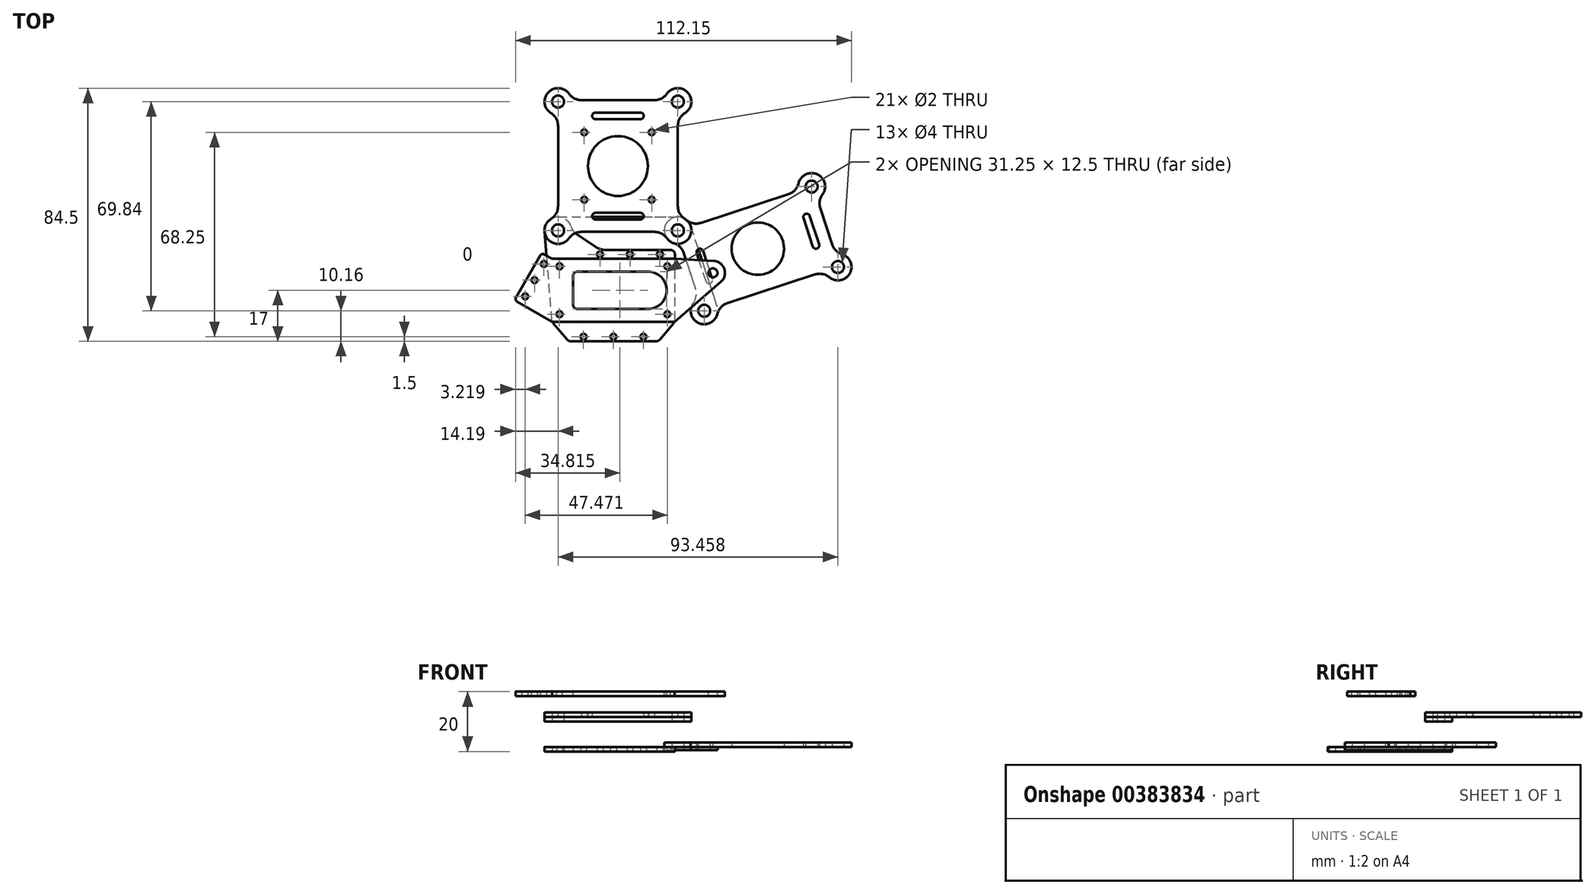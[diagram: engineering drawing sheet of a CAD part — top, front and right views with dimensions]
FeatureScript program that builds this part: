
annotation { "Feature Type Name" : "Feature", "Feature Type Description" : "" }
export const myFeature = defineFeature(function(context is Context, id is Id, definition is map)
    precondition{}
    {
        {
            var Q0;
            Q0=qCreatedBy(makeId("Top.planeOp"),FACE);
            var sketch = newSketch(context, id + "F0", { "sketchPlane" : qUnion([Q0])});
            skArc(sketch, "E0", {"start": v(0, -6.25) * mm, "mid": v(6.25, 0) * mm, "end": v(0, 6.25) * mm});
            skCircle(sketch, "E1", {"center": v(6.5, 8) * mm, "radius": 1 * mm});
            skLineSegment(sketch, "E2", {"start": v(6.5, 8) * mm, "end": v(-29.5, 8) * mm, "construction": true});
            skPoint(sketch, "E3", {"position": v(-11.5, 8) * mm});
            skCircle(sketch, "E4", {"center": v(-29.5, 8) * mm, "radius": 1 * mm});
            skCircle(sketch, "E5.MirrorC", {"center": v(-29.5, -8) * mm, "radius": 1 * mm});
            skCircle(sketch, "E6.MirrorC", {"center": v(6.5, -8) * mm, "radius": 1 * mm});
            skLineSegment(sketch, "E7.bottom", {"start": v(-32, 10.5) * mm, "end": v(9, 10.5) * mm});
            skLineSegment(sketch, "E7.top", {"start": v(-32, -10.5) * mm, "end": v(9, -10.5) * mm});
            skLineSegment(sketch, "E7.left", {"start": v(-32, 10.5) * mm, "end": v(-32, -10.5) * mm});
            skLineSegment(sketch, "E7.right", {"start": v(9, 10.5) * mm, "end": v(9, -10.5) * mm});
            skPoint(sketch, "E7.middle", {"position": v(-11.5, 0) * mm});
            skLineSegment(sketch, "E8", {"start": v(0, 0) * mm, "end": v(18.8, -6.84) * mm, "construction": true});
            skCircle(sketch, "E9", {"center": v(-30, 20) * mm, "radius": 2 * mm});
            skLineSegment(sketch, "E10", {"start": v(-30, 20) * mm, "end": v(10, 20) * mm, "construction": true});
            skLineSegment(sketch, "E11", {"start": v(10, 20) * mm, "end": v(18.8, -6.84) * mm, "construction": true});
            skCircle(sketch, "E12", {"center": v(10, 20) * mm, "radius": 2 * mm});
            skCircle(sketch, "E13", {"center": v(18.8, -6.84) * mm, "radius": 2 * mm});
            skCircle(sketch, "E14", {"center": v(18.8, -6.84) * mm, "radius": 4.5 * mm});
            skCircle(sketch, "E15", {"center": v(10, 20) * mm, "radius": 4.5 * mm});
            skLineSegment(sketch, "E16", {"start": v(10, 20) * mm, "end": v(14.28, 21.4) * mm, "construction": true});
            skLineSegment(sketch, "E17", {"start": v(14.28, 21.4) * mm, "end": v(23.07, -5.44) * mm});
            skLineSegment(sketch, "E18", {"start": v(10.92, 15.6) * mm, "end": v(16.93, -2.75) * mm});
            skCircle(sketch, "E19", {"center": v(-30, 20) * mm, "radius": 4.5 * mm});
            skLineSegment(sketch, "E20", {"start": v(-32, -10.5) * mm, "end": v(-34.48, 19.63) * mm});
            skLineSegment(sketch, "E21", {"start": v(-15.92, 13.5) * mm, "end": v(-25.5, 20) * mm});
            skLineSegment(sketch, "E22", {"start": v(0, 6.25) * mm, "end": v(-23.5, 6.25) * mm});
            skLineSegment(sketch, "E23", {"start": v(-25, 4.75) * mm, "end": v(-25, 0) * mm});
            skLineSegment(sketch, "E24.MirrorCS", {"start": v(-25, -4.75) * mm, "end": v(-25, 0) * mm});
            skLineSegment(sketch, "E25.MirrorCS", {"start": v(0, -6.25) * mm, "end": v(-23.5, -6.25) * mm});
            skPoint(sketch, "E26.visualSharp", {"position": v(-25, 6.25) * mm});
            skArc(sketch, "E26.filletArc", {"start": v(-23.5, 6.25) * mm, "mid": v(-24.56, 5.81) * mm, "end": v(-25, 4.75) * mm});
            skPoint(sketch, "E27.visualSharp", {"position": v(-25, -6.25) * mm});
            skArc(sketch, "E27.filletArc", {"start": v(-25, -4.75) * mm, "mid": v(-24.56, -5.81) * mm, "end": v(-23.5, -6.25) * mm});
            skPoint(sketch, "E28.visualSharp", {"position": v(0, 6.25) * mm});
            skLineSegment(sketch, "E28.filletArc", {"start": v(0, 6.25) * mm, "end": v(0, 6.25) * mm});
            skPoint(sketch, "E29.visualSharp", {"position": v(0, -6.25) * mm});
            skLineSegment(sketch, "E29.filletArc", {"start": v(0, -6.25) * mm, "end": v(0, -6.25) * mm});
            skLineSegment(sketch, "E30.bottom", {"start": v(-26.5, -10.5) * mm, "end": v(3.5, -10.5) * mm});
            skLineSegment(sketch, "E30.top", {"start": v(-26.5, -17) * mm, "end": v(3.5, -17) * mm});
            skLineSegment(sketch, "E30.left", {"start": v(-26.5, -10.5) * mm, "end": v(-26.5, -17) * mm});
            skLineSegment(sketch, "E30.right", {"start": v(3.5, -10.5) * mm, "end": v(3.5, -17) * mm});
            skPoint(sketch, "E30.middle", {"position": v(-11.5, -13.75) * mm});
            skLineSegment(sketch, "E31", {"start": v(-32, -10.5) * mm, "end": v(-26.5, -17) * mm});
            skLineSegment(sketch, "E32", {"start": v(3.5, -17) * mm, "end": v(9, -10.5) * mm});
            skLineSegment(sketch, "E33", {"start": v(-11.5, -10.5) * mm, "end": v(-11.5, -17) * mm, "construction": true});
            skCircle(sketch, "E34", {"center": v(4, 12) * mm, "radius": 1 * mm});
            skCircle(sketch, "E35", {"center": v(-6, 12) * mm, "radius": 1 * mm});
            skCircle(sketch, "E36", {"center": v(-16, 12) * mm, "radius": 1 * mm});
            skLineSegment(sketch, "E37", {"start": v(9, 10.5) * mm, "end": v(9, 13.5) * mm});
            skLineSegment(sketch, "E38", {"start": v(9, 13.5) * mm, "end": v(-15.92, 13.5) * mm});
            skPoint(sketch, "E39.orphan", {"position": v(-11.5, 10.5) * mm});
            skCircle(sketch, "E40", {"center": v(-11.5, -15.5) * mm, "radius": 1 * mm});
            skCircle(sketch, "E41", {"center": v(-1.5, -15.5) * mm, "radius": 1 * mm});
            skCircle(sketch, "E42.MirrorC", {"center": v(-21.5, -15.5) * mm, "radius": 1 * mm});
            skSolve(sketch);
        }
        {
            var Q0;
            Q0=qSketchRegion(id+"F0",true);
            extrude(context, id + "F1", {"entities" : qUnion([Q0]), "depth" : 1.5 * mm, "offsetDistance" : 25 * mm});
        }
        {
            var Q0;
            Q0=qCreatedBy(makeId("Top.planeOp"),FACE);
            cPlane(context, id + "F2", {"entities" : qUnion([Q0]), "cplaneType" : CPlaneType.OFFSET, "offset" : 10 * mm, "width" : 150 * mm, "height" : 150 * mm});
        }
        {
            var Q0;
            Q0=qCreatedBy(id+"F2.planeOp",FACE);
            var sketch = newSketch(context, id + "F3", { "sketchPlane" : qUnion([Q0])});
            skCircle(sketch, "E43.0", {"center": v(10, 20) * mm, "radius": 2 * mm});
            skCircle(sketch, "E44.0", {"center": v(-30, 20) * mm, "radius": 2 * mm});
            skArc(sketch, "E45", {"start": v(-30, 24.5) * mm, "mid": v(-33.35, 17) * mm, "end": v(-25.53, 19.5) * mm});
            skArc(sketch, "E46", {"start": v(5.53, 19.5) * mm, "mid": v(13.35, 17) * mm, "end": v(10, 24.5) * mm});
            skLineSegment(sketch, "E47", {"start": v(-30, 24.5) * mm, "end": v(10, 24.5) * mm});
            skLineSegment(sketch, "E48", {"start": v(-25.53, 19.5) * mm, "end": v(5.53, 19.5) * mm});
            skSolve(sketch);
        }
        {
            var Q0;
            Q0=qSketchRegion(id+"F3",true);
            extrude(context, id + "F4", {"entities" : qUnion([Q0]), "depth" : 1.5 * mm, "offsetDistance" : 25 * mm});
        }
        {
            var Q0;
            Q0=makeQuery(id+"F1.opExtrude","SWEPT_EDGE",EDGE,{"disambiguationData":[OSD([sQuery(id+"F0.wireOp",EDGE,"E15"),sQuery(id+"F0.wireOp",EDGE,"E18")])]});
            var Q1;
            Q1=makeQuery(id+"F1.opExtrude","SWEPT_EDGE",EDGE,{"disambiguationData":[OSD([sQuery(id+"F0.wireOp",EDGE,"E14"),sQuery(id+"F0.wireOp",EDGE,"E18")])]});
            var Q2;
            Q2=makeQuery(id+"F4.opExtrude","SWEPT_EDGE",EDGE,{"disambiguationData":[OSD([sQuery(id+"F3.wireOp",EDGE,"E45"),sQuery(id+"F3.wireOp",EDGE,"E48")])]});
            var Q3;
            Q3=makeQuery(id+"F4.opExtrude","SWEPT_EDGE",EDGE,{"disambiguationData":[OSD([sQuery(id+"F3.wireOp",EDGE,"E46"),sQuery(id+"F3.wireOp",EDGE,"E48")])]});
            var Q4;
            Q4=makeQuery(id+"F1.opExtrude","SWEPT_EDGE",EDGE,{"disambiguationData":[OSD([sQuery(id+"F0.wireOp",EDGE,"E19"),sQuery(id+"F0.wireOp",EDGE,"E21")])]});
            var Q5;
            Q5=makeQuery(id+"F1.opExtrude","SWEPT_EDGE",EDGE,{"disambiguationData":[OSD([sQuery(id+"F0.wireOp",EDGE,"E7.bottom"),sQuery(id+"F0.wireOp",EDGE,"E21")])]});
            fillet(context, id + "F5", {"entities" : qUnion([Q0, Q1, Q2, Q3, Q4, Q5]), "radius" : 5 * mm, "tangentPropagation" : true, "allowEdgeOverflow" : false});
        }
        {
            var Q0;
            Q0=makeQuery(id+"F1.opExtrude","SWEPT_EDGE",EDGE,{"disambiguationData":[OSD([sQuery(id+"F0.wireOp",EDGE,"E7.bottom"),sQuery(id+"F0.wireOp",EDGE,"E7.right")])]});
            var Q1;
            Q1=makeQuery(id+"F1.opExtrude","SWEPT_EDGE",EDGE,{"disambiguationData":[OSD([sQuery(id+"F0.wireOp",EDGE,"E7.top"),sQuery(id+"F0.wireOp",EDGE,"E7.left"),sQuery(id+"F0.wireOp",EDGE,"E20")])]});
            var Q2;
            Q2=makeQuery(id+"F1.opExtrude","SWEPT_EDGE",EDGE,{"disambiguationData":[OSD([sQuery(id+"F0.wireOp",EDGE,"E7.top"),sQuery(id+"F0.wireOp",EDGE,"E7.right")])]});
            var Q3;
            Q3=makeQuery(id+"F1.opExtrude","SWEPT_EDGE",EDGE,{"disambiguationData":[OSD([sQuery(id+"F0.wireOp",EDGE,"E30.top"),sQuery(id+"F0.wireOp",EDGE,"E30.left"),sQuery(id+"F0.wireOp",EDGE,"E31")])]});
            var Q4;
            Q4=makeQuery(id+"F1.opExtrude","SWEPT_EDGE",EDGE,{"disambiguationData":[OSD([sQuery(id+"F0.wireOp",EDGE,"E30.top"),sQuery(id+"F0.wireOp",EDGE,"E30.right"),sQuery(id+"F0.wireOp",EDGE,"E32")])]});
            var Q5;
            Q5=makeQuery(id+"F1.opExtrude","SWEPT_EDGE",EDGE,{"disambiguationData":[OSD([sQuery(id+"F0.wireOp",EDGE,"E37"),sQuery(id+"F0.wireOp",EDGE,"E38")])]});
            fillet(context, id + "F6", {"entities" : qUnion([Q0, Q1, Q2, Q3, Q4, Q5]), "radius" : 1.5 * mm, "tangentPropagation" : true, "allowEdgeOverflow" : false});
        }
        {
            var Q0;
            Q0=makeQuery(id+"F1.opExtrude","CAP_FACE",FACE,{"disambiguationData":[OSD([sQuery(id+"F0.wireOp",EDGE,"E12"),sQuery(id+"F0.wireOp",EDGE,"E13"),sQuery(id+"F0.wireOp",EDGE,"E14"),sQuery(id+"F0.wireOp",EDGE,"E15"),sQuery(id+"F0.wireOp",EDGE,"E17"),sQuery(id+"F0.wireOp",EDGE,"E18")])],"isStart":true});
            extrude(context, id + "F7", {"entities" : qUnion([Q0]), "operationType" : NewBodyOperationType.REMOVE, "oppositeDirection" : true, "depth" : 0.5 * mm, "offsetDistance" : 25 * mm});
        }
        {
            var Q0;
            Q0=makeQuery(id+"F1.opExtrude","CAP_FACE",FACE,{"disambiguationData":[OSD([sQuery(id+"F0.wireOp",EDGE,"E12"),sQuery(id+"F0.wireOp",EDGE,"E13"),sQuery(id+"F0.wireOp",EDGE,"E14"),sQuery(id+"F0.wireOp",EDGE,"E15"),sQuery(id+"F0.wireOp",EDGE,"E17"),sQuery(id+"F0.wireOp",EDGE,"E18")])],"isStart":false});
            var sketch = newSketch(context, id + "F8", { "sketchPlane" : qUnion([Q0])});
            skLineSegment(sketch, "E49", {"start": v(13.92, 6.42) * mm, "end": v(36.73, 13.9) * mm, "construction": true});
            skLineSegment(sketch, "E50", {"start": v(36.73, 13.9) * mm, "end": v(41.13, 0.48) * mm, "construction": true});
            skLineSegment(sketch, "E51", {"start": v(23.07, -5.44) * mm, "end": v(41.13, 0.48) * mm});
            skPoint(sketch, "E52", {"position": v(18.8, -6.84) * mm});
            skLineSegment(sketch, "E53", {"start": v(18.8, -6.84) * mm, "end": v(23.07, -5.44) * mm, "construction": true});
            skLineSegment(sketch, "E54.MirrorCS", {"start": v(14.28, 21.4) * mm, "end": v(32.33, 27.32) * mm});
            skArc(sketch, "E55.0.0", {"start": v(14.28, 21.4) * mm, "mid": v(6.8, 23.16) * mm, "end": v(8.67, 15.7) * mm});
            skArc(sketch, "E55.0.1", {"start": v(8.67, 15.7) * mm, "mid": v(10.7, 14.49) * mm, "end": v(11.94, 12.48) * mm});
            skLineSegment(sketch, "E55.0.2", {"start": v(11.94, 12.48) * mm, "end": v(15.9, 0.36) * mm});
            skArc(sketch, "E55.0.3", {"start": v(15.9, 0.36) * mm, "mid": v(16.1, -1.99) * mm, "end": v(15.18, -4.16) * mm});
            skArc(sketch, "E55.0.4", {"start": v(15.18, -4.16) * mm, "mid": v(18.08, -11.28) * mm, "end": v(23.07, -5.44) * mm});
            skLineSegment(sketch, "E55.0.5", {"start": v(23.07, -5.44) * mm, "end": v(14.28, 21.4) * mm});
            skLineSegment(sketch, "E56.MirrorCS", {"start": v(57.55, 27.43) * mm, "end": v(61.52, 15.3) * mm});
            skArc(sketch, "E57.MirrorCS", {"start": v(58.28, 31.96) * mm, "mid": v(57.37, 29.78) * mm, "end": v(57.55, 27.43) * mm});
            skArc(sketch, "E58.MirrorCS", {"start": v(50.39, 33.23) * mm, "mid": v(55.38, 39.08) * mm, "end": v(58.28, 31.96) * mm});
            skLineSegment(sketch, "E59.MirrorCS", {"start": v(50.39, 33.23) * mm, "end": v(32.33, 27.32) * mm});
            skLineSegment(sketch, "E60.MirrorCS", {"start": v(63.46, 7.8) * mm, "end": v(59.18, 6.4) * mm, "construction": true});
            skLineSegment(sketch, "E61.MirrorCS", {"start": v(59.18, 6.4) * mm, "end": v(41.13, 0.48) * mm});
            skLineSegment(sketch, "E62.MirrorCS", {"start": v(59.54, 21.37) * mm, "end": v(36.73, 13.9) * mm, "construction": true});
            skArc(sketch, "E63.MirrorCS", {"start": v(61.52, 15.3) * mm, "mid": v(62.77, 13.3) * mm, "end": v(64.8, 12.1) * mm});
            skPoint(sketch, "E64.MirrorP", {"position": v(63.46, 7.8) * mm});
            skArc(sketch, "E65.MirrorCS", {"start": v(64.8, 12.1) * mm, "mid": v(66.66, 4.64) * mm, "end": v(59.18, 6.4) * mm});
            skLineSegment(sketch, "E66.MirrorCS", {"start": v(59.18, 6.4) * mm, "end": v(59.18, 6.4) * mm});
            skCircle(sketch, "E67.0", {"center": v(10, 20) * mm, "radius": 2 * mm});
            skCircle(sketch, "E68.0", {"center": v(18.8, -6.84) * mm, "radius": 2 * mm});
            skCircle(sketch, "E69.MirrorC", {"center": v(54.66, 34.63) * mm, "radius": 2 * mm});
            skCircle(sketch, "E70.MirrorC", {"center": v(63.46, 7.8) * mm, "radius": 2 * mm});
            skCircle(sketch, "E71", {"center": v(36.73, 13.9) * mm, "radius": 8.75 * mm});
            skLineSegment(sketch, "E72.trimOffspring", {"start": v(59.18, 6.4) * mm, "end": v(50.39, 33.23) * mm});
            skLineSegment(sketch, "E73.trimOffspring", {"start": v(14.28, 21.4) * mm, "end": v(14.28, 21.4) * mm});
            skCircle(sketch, "E74", {"center": v(53, 24.49) * mm, "radius": 1.1 * mm});
            skLineSegment(sketch, "E75", {"start": v(53, 24.49) * mm, "end": v(51.94, 24.14) * mm, "construction": true});
            skLineSegment(sketch, "E76", {"start": v(51.94, 24.14) * mm, "end": v(53.5, 19.4) * mm});
            skLineSegment(sketch, "E77", {"start": v(53, 24.49) * mm, "end": v(54.55, 19.73) * mm, "construction": true});
            skLineSegment(sketch, "E78.MirrorCS", {"start": v(54.04, 24.83) * mm, "end": v(55.6, 20.08) * mm});
            skLineSegment(sketch, "E79.MirrorCS", {"start": v(57.15, 15.33) * mm, "end": v(55.6, 20.08) * mm});
            skLineSegment(sketch, "E80.MirrorCS", {"start": v(55.06, 14.64) * mm, "end": v(53.5, 19.4) * mm});
            skCircle(sketch, "E81.MirrorC", {"center": v(56.1, 14.98) * mm, "radius": 1.1 * mm});
            skLineSegment(sketch, "E82.MirrorCS", {"start": v(56.1, 14.98) * mm, "end": v(54.55, 19.73) * mm, "construction": true});
            skLineSegment(sketch, "E83.MirrorCS", {"start": v(56.1, 14.98) * mm, "end": v(55.06, 14.64) * mm, "construction": true});
            skLineSegment(sketch, "E84.MirrorCS", {"start": v(17.35, 12.81) * mm, "end": v(18.4, 13.15) * mm, "construction": true});
            skLineSegment(sketch, "E85.MirrorCS", {"start": v(20.47, 3.3) * mm, "end": v(21.51, 3.65) * mm, "construction": true});
            skLineSegment(sketch, "E86.MirrorCS", {"start": v(19.42, 2.96) * mm, "end": v(17.87, 7.72) * mm});
            skCircle(sketch, "E87.MirrorC", {"center": v(17.35, 12.81) * mm, "radius": 1.1 * mm});
            skCircle(sketch, "E88.MirrorC", {"center": v(20.47, 3.3) * mm, "radius": 1.1 * mm});
            skLineSegment(sketch, "E89.MirrorCS", {"start": v(16.3, 12.47) * mm, "end": v(17.87, 7.72) * mm});
            skLineSegment(sketch, "E90.MirrorCS", {"start": v(18.4, 13.15) * mm, "end": v(19.96, 8.4) * mm});
            skLineSegment(sketch, "E91.MirrorCS", {"start": v(17.35, 12.81) * mm, "end": v(18.91, 8.06) * mm, "construction": true});
            skLineSegment(sketch, "E92.MirrorCS", {"start": v(20.47, 3.3) * mm, "end": v(18.91, 8.06) * mm, "construction": true});
            skLineSegment(sketch, "E93.MirrorCS", {"start": v(21.51, 3.65) * mm, "end": v(19.96, 8.4) * mm});
            skSolve(sketch);
        }
        {
            var Q0;
            Q0=qSketchRegion(id+"F8",true);
            extrude(context, id + "F9", {"entities" : qUnion([Q0]), "depth" : 1.5 * mm, "offsetDistance" : 25 * mm});
        }
        {
            var Q0;
            Q0=makeQuery(id+"F4.opExtrude","CAP_FACE",FACE,{"disambiguationData":[OSD([sQuery(id+"F3.wireOp",EDGE,"E43.0"),sQuery(id+"F3.wireOp",EDGE,"E44.0"),sQuery(id+"F3.wireOp",EDGE,"E45"),sQuery(id+"F3.wireOp",EDGE,"E46"),sQuery(id+"F3.wireOp",EDGE,"E47"),sQuery(id+"F3.wireOp",EDGE,"E48")])],"isStart":false});
            var sketch = newSketch(context, id + "F10", { "sketchPlane" : qUnion([Q0])});
            skLineSegment(sketch, "E94", {"start": v(-10, 24.5) * mm, "end": v(-10, 41.5) * mm, "construction": true});
            skArc(sketch, "E95.0.0", {"start": v(-30, 24.5) * mm, "mid": v(-34, 17.94) * mm, "end": v(-26.33, 17.4) * mm});
            skArc(sketch, "E95.0.1", {"start": v(-26.33, 17.4) * mm, "mid": v(-24.55, 18.94) * mm, "end": v(-22.25, 19.5) * mm});
            skLineSegment(sketch, "E95.0.2", {"start": v(-22.25, 19.5) * mm, "end": v(2.25, 19.5) * mm});
            skArc(sketch, "E95.0.3", {"start": v(2.25, 19.5) * mm, "mid": v(4.55, 18.94) * mm, "end": v(6.33, 17.4) * mm});
            skArc(sketch, "E95.0.4", {"start": v(6.33, 17.4) * mm, "mid": v(14, 17.94) * mm, "end": v(10, 24.5) * mm});
            skLineSegment(sketch, "E95.0.5", {"start": v(10, 24.5) * mm, "end": v(-30, 24.5) * mm});
            skCircle(sketch, "E96.0", {"center": v(-30, 20) * mm, "radius": 2 * mm});
            skCircle(sketch, "E97.0", {"center": v(10, 20) * mm, "radius": 2 * mm});
            skLineSegment(sketch, "E98", {"start": v(-10, 41.5) * mm, "end": v(10, 41.5) * mm, "construction": true});
            skCircle(sketch, "E99.MirrorC", {"center": v(10, 63) * mm, "radius": 2 * mm});
            skArc(sketch, "E100.MirrorCS", {"start": v(-30, 58.5) * mm, "mid": v(-34, 65.06) * mm, "end": v(-26.33, 65.6) * mm});
            skArc(sketch, "E101.MirrorCS", {"start": v(-26.33, 65.6) * mm, "mid": v(-24.55, 64.06) * mm, "end": v(-22.25, 63.5) * mm});
            skLineSegment(sketch, "E102.MirrorCS", {"start": v(-22.25, 63.5) * mm, "end": v(2.25, 63.5) * mm});
            skArc(sketch, "E103.MirrorCS", {"start": v(2.25, 63.5) * mm, "mid": v(4.55, 64.06) * mm, "end": v(6.33, 65.6) * mm});
            skArc(sketch, "E104.MirrorCS", {"start": v(6.33, 65.6) * mm, "mid": v(14, 65.06) * mm, "end": v(10, 58.5) * mm});
            skCircle(sketch, "E105.MirrorC", {"center": v(-30, 63) * mm, "radius": 2 * mm});
            skLineSegment(sketch, "E106.MirrorCS", {"start": v(10, 58.5) * mm, "end": v(-30, 58.5) * mm});
            skLineSegment(sketch, "E107", {"start": v(10, 58.5) * mm, "end": v(10, 24.5) * mm});
            skLineSegment(sketch, "E108.MirrorCS", {"start": v(-30, 58.5) * mm, "end": v(-30, 24.5) * mm});
            skCircle(sketch, "E109", {"center": v(-10, 41.5) * mm, "radius": 10 * mm});
            skLineSegment(sketch, "E110", {"start": v(-30, 58.25) * mm, "end": v(10, 58.25) * mm, "construction": true});
            skCircle(sketch, "E111", {"center": v(-17.5, 58.25) * mm, "radius": 1.1 * mm});
            skLineSegment(sketch, "E112", {"start": v(-10, 57.15) * mm, "end": v(-17.5, 57.15) * mm});
            skLineSegment(sketch, "E113.MirrorCS", {"start": v(-10, 59.35) * mm, "end": v(-17.5, 59.35) * mm});
            skLineSegment(sketch, "E114.MirrorCS", {"start": v(-10, 59.35) * mm, "end": v(-2.5, 59.35) * mm});
            skCircle(sketch, "E115.MirrorC", {"center": v(-2.5, 58.25) * mm, "radius": 1.1 * mm});
            skLineSegment(sketch, "E116.MirrorCS", {"start": v(-10, 57.15) * mm, "end": v(-2.5, 57.15) * mm});
            skLineSegment(sketch, "E117.MirrorCS", {"start": v(-10, 23.65) * mm, "end": v(-17.5, 23.65) * mm});
            skCircle(sketch, "E118.MirrorC", {"center": v(-17.5, 24.75) * mm, "radius": 1.1 * mm});
            skLineSegment(sketch, "E119.MirrorCS", {"start": v(-10, 25.85) * mm, "end": v(-17.5, 25.85) * mm});
            skLineSegment(sketch, "E120.MirrorCS", {"start": v(-10, 23.65) * mm, "end": v(-2.5, 23.65) * mm});
            skLineSegment(sketch, "E121.MirrorCS", {"start": v(-10, 25.85) * mm, "end": v(-2.5, 25.85) * mm});
            skCircle(sketch, "E122.MirrorC", {"center": v(-2.5, 24.75) * mm, "radius": 1.1 * mm});
            skLineSegment(sketch, "E123.bottom", {"start": v(-21.25, 52.75) * mm, "end": v(1.25, 52.75) * mm, "construction": true});
            skLineSegment(sketch, "E123.top", {"start": v(-21.25, 30.25) * mm, "end": v(1.25, 30.25) * mm, "construction": true});
            skLineSegment(sketch, "E123.left", {"start": v(-21.25, 52.75) * mm, "end": v(-21.25, 30.25) * mm, "construction": true});
            skLineSegment(sketch, "E123.right", {"start": v(1.25, 52.75) * mm, "end": v(1.25, 30.25) * mm, "construction": true});
            skCircle(sketch, "E124", {"center": v(-21.25, 52.75) * mm, "radius": 1 * mm});
            skCircle(sketch, "E125.MirrorC", {"center": v(-21.25, 30.25) * mm, "radius": 1 * mm});
            skCircle(sketch, "E126.MirrorC", {"center": v(1.25, 52.75) * mm, "radius": 1 * mm});
            skCircle(sketch, "E127.MirrorC", {"center": v(1.25, 30.25) * mm, "radius": 1 * mm});
            skSolve(sketch);
        }
        {
            var Q0;
            Q0=qSketchRegion(id+"F10",true);
            extrude(context, id + "F11", {"entities" : qUnion([Q0]), "depth" : 1.5 * mm, "offsetDistance" : 25 * mm});
        }
        {
            var Q0;
            Q0=makeQuery(id+"F9.opExtrude","SWEPT_EDGE",EDGE,{"disambiguationData":[OSD([sQuery(id+"F8.wireOp",EDGE,"E51"),sQuery(id+"F8.wireOp",EDGE,"E55.0.4"),sQuery(id+"F8.wireOp",EDGE,"E55.0.5")])]});
            var Q1;
            Q1=makeQuery(id+"F9.opExtrude","SWEPT_EDGE",EDGE,{"disambiguationData":[OSD([sQuery(id+"F8.wireOp",EDGE,"E61.MirrorCS"),sQuery(id+"F8.wireOp",EDGE,"E65.MirrorCS"),sQuery(id+"F8.wireOp",EDGE,"E72.trimOffspring")])]});
            var Q2;
            Q2=makeQuery(id+"F9.opExtrude","SWEPT_EDGE",EDGE,{"disambiguationData":[OSD([sQuery(id+"F8.wireOp",EDGE,"E58.MirrorCS"),sQuery(id+"F8.wireOp",EDGE,"E59.MirrorCS"),sQuery(id+"F8.wireOp",EDGE,"E72.trimOffspring")])]});
            var Q3;
            Q3=makeQuery(id+"F9.opExtrude","SWEPT_EDGE",EDGE,{"disambiguationData":[OSD([sQuery(id+"F8.wireOp",EDGE,"E54.MirrorCS"),sQuery(id+"F8.wireOp",EDGE,"E55.0.0"),sQuery(id+"F8.wireOp",EDGE,"E55.0.5")])]});
            var Q4;
            Q4=makeQuery(id+"F11.opExtrude","SWEPT_EDGE",EDGE,{"disambiguationData":[OSD([sQuery(id+"F10.wireOp",EDGE,"E104.MirrorCS"),sQuery(id+"F10.wireOp",EDGE,"E106.MirrorCS"),sQuery(id+"F10.wireOp",EDGE,"E107")])]});
            var Q5;
            Q5=makeQuery(id+"F11.opExtrude","SWEPT_EDGE",EDGE,{"disambiguationData":[OSD([sQuery(id+"F10.wireOp",EDGE,"E95.0.4"),sQuery(id+"F10.wireOp",EDGE,"E95.0.5"),sQuery(id+"F10.wireOp",EDGE,"E107")])]});
            var Q6;
            Q6=makeQuery(id+"F11.opExtrude","SWEPT_EDGE",EDGE,{"disambiguationData":[OSD([sQuery(id+"F10.wireOp",EDGE,"E95.0.0"),sQuery(id+"F10.wireOp",EDGE,"E95.0.5"),sQuery(id+"F10.wireOp",EDGE,"E108.MirrorCS")])]});
            var Q7;
            Q7=makeQuery(id+"F11.opExtrude","SWEPT_EDGE",EDGE,{"disambiguationData":[OSD([sQuery(id+"F10.wireOp",EDGE,"E100.MirrorCS"),sQuery(id+"F10.wireOp",EDGE,"E106.MirrorCS"),sQuery(id+"F10.wireOp",EDGE,"E108.MirrorCS")])]});
            fillet(context, id + "F12", {"entities" : qUnion([Q0, Q1, Q2, Q3, Q4, Q5, Q6, Q7]), "radius" : 5 * mm, "tangentPropagation" : true, "allowEdgeOverflow" : false});
        }
        {
            var Q0;
            Q0=makeQuery(id+"F1.opExtrude","SWEPT_BODY",BODY,{"disambiguationData":[OSD([sQuery(id+"F0.wireOp",EDGE,"E0"),sQuery(id+"F0.wireOp",EDGE,"E1"),sQuery(id+"F0.wireOp",EDGE,"E4"),sQuery(id+"F0.wireOp",EDGE,"E5.MirrorC"),sQuery(id+"F0.wireOp",EDGE,"E6.MirrorC"),sQuery(id+"F0.wireOp",EDGE,"E7.right"),sQuery(id+"F0.wireOp",EDGE,"E9"),sQuery(id+"F0.wireOp",EDGE,"E19"),sQuery(id+"F0.wireOp",EDGE,"E20"),sQuery(id+"F0.wireOp",EDGE,"E21"),sQuery(id+"F0.wireOp",EDGE,"E22"),sQuery(id+"F0.wireOp",EDGE,"E23"),sQuery(id+"F0.wireOp",EDGE,"E24.MirrorCS"),sQuery(id+"F0.wireOp",EDGE,"E25.MirrorCS"),sQuery(id+"F0.wireOp",EDGE,"E26.filletArc"),sQuery(id+"F0.wireOp",EDGE,"E27.filletArc"),sQuery(id+"F0.wireOp",EDGE,"E30.top"),sQuery(id+"F0.wireOp",EDGE,"E31"),sQuery(id+"F0.wireOp",EDGE,"E32"),sQuery(id+"F0.wireOp",EDGE,"E34"),sQuery(id+"F0.wireOp",EDGE,"E35"),sQuery(id+"F0.wireOp",EDGE,"E36"),sQuery(id+"F0.wireOp",EDGE,"E37"),sQuery(id+"F0.wireOp",EDGE,"E38"),sQuery(id+"F0.wireOp",EDGE,"E40"),sQuery(id+"F0.wireOp",EDGE,"E41"),sQuery(id+"F0.wireOp",EDGE,"E42.MirrorC")])]});
            var Q1;
            Q1=qCreatedBy(id+"F2.planeOp",FACE);
            mirror(context, id + "F13", {"entities" : qUnion([Q0]), "mirrorPlane" : qUnion([Q1])});
        }
        {
            var Q0;
            Q0=makeQuery(id+"F13.opPattern","COPY",FACE,{"derivedFrom":makeQuery(id+"F1.opExtrude","CAP_FACE",FACE,{"disambiguationData":[OSD([sQuery(id+"F0.wireOp",EDGE,"E0"),sQuery(id+"F0.wireOp",EDGE,"E1"),sQuery(id+"F0.wireOp",EDGE,"E4"),sQuery(id+"F0.wireOp",EDGE,"E5.MirrorC"),sQuery(id+"F0.wireOp",EDGE,"E6.MirrorC"),sQuery(id+"F0.wireOp",EDGE,"E7.right"),sQuery(id+"F0.wireOp",EDGE,"E9"),sQuery(id+"F0.wireOp",EDGE,"E19"),sQuery(id+"F0.wireOp",EDGE,"E20"),sQuery(id+"F0.wireOp",EDGE,"E21"),sQuery(id+"F0.wireOp",EDGE,"E22"),sQuery(id+"F0.wireOp",EDGE,"E23"),sQuery(id+"F0.wireOp",EDGE,"E24.MirrorCS"),sQuery(id+"F0.wireOp",EDGE,"E25.MirrorCS"),sQuery(id+"F0.wireOp",EDGE,"E26.filletArc"),sQuery(id+"F0.wireOp",EDGE,"E27.filletArc"),sQuery(id+"F0.wireOp",EDGE,"E30.top"),sQuery(id+"F0.wireOp",EDGE,"E31"),sQuery(id+"F0.wireOp",EDGE,"E32"),sQuery(id+"F0.wireOp",EDGE,"E34"),sQuery(id+"F0.wireOp",EDGE,"E35"),sQuery(id+"F0.wireOp",EDGE,"E36"),sQuery(id+"F0.wireOp",EDGE,"E37"),sQuery(id+"F0.wireOp",EDGE,"E38"),sQuery(id+"F0.wireOp",EDGE,"E40"),sQuery(id+"F0.wireOp",EDGE,"E41"),sQuery(id+"F0.wireOp",EDGE,"E42.MirrorC")])],"isStart":true}),"instanceName":"1"});
            var sketch = newSketch(context, id + "F14", { "sketchPlane" : qUnion([Q0])});
            skLineSegment(sketch, "E128.bottom", {"start": v(9, 10.5) * mm, "end": v(-32, 10.5) * mm});
            skLineSegment(sketch, "E128.top", {"start": v(9, -10.5) * mm, "end": v(-32, -10.5) * mm});
            skLineSegment(sketch, "E128.left", {"start": v(9, 10.5) * mm, "end": v(9, -10.5) * mm});
            skLineSegment(sketch, "E128.right", {"start": v(-32, 10.5) * mm, "end": v(-32, -10.5) * mm});
            skPoint(sketch, "E128.middle", {"position": v(-11.5, 0) * mm});
            skPoint(sketch, "E129", {"position": v(6.5, -8) * mm});
            skSolve(sketch);
        }
        {
            var Q0;
            {var subQ12=sQuery(id+"F14.wireOp",EDGE,"E128.bottom");Q0=makeQuery(id+"F14.imprint","IMPRINT",FACE,{"disambiguationData":[TD([[makeQuery(id+"F14.imprint","IMPRINT",EDGE,{"derivedFrom":subQ12}),-1.0]])]});}
            var Q1;
            {var subQ4=sQuery(id+"F0.wireOp",EDGE,"E40");Q1=makeQuery(id+"F14.imprint","IMPRINT",FACE,{"disambiguationData":[TD([[makeQuery(id+"F14.imprint","IMPRINT",EDGE,{"derivedFrom":makeQuery(id+"F13.opPattern","COPY",EDGE,{"derivedFrom":makeQuery(id+"F1.opExtrude","CAP_EDGE",EDGE,{"disambiguationData":[OSD([subQ4])],"isStart":true}),"instanceName":"1"})}),-1.0]])]});}
            extrude(context, id + "F15", {"entities" : qUnion([Q0, Q1]), "operationType" : NewBodyOperationType.REMOVE, "endBound" : BoundingType.UP_TO_NEXT, "oppositeDirection" : true, "depth" : 25 * mm, "offsetDistance" : 25 * mm});
        }
        {
            var Q0;
            Q0=makeQuery(id+"F13.opPattern","COPY",FACE,{"derivedFrom":makeQuery(id+"F1.opExtrude","CAP_FACE",FACE,{"disambiguationData":[OSD([sQuery(id+"F0.wireOp",EDGE,"E0"),sQuery(id+"F0.wireOp",EDGE,"E1"),sQuery(id+"F0.wireOp",EDGE,"E4"),sQuery(id+"F0.wireOp",EDGE,"E5.MirrorC"),sQuery(id+"F0.wireOp",EDGE,"E6.MirrorC"),sQuery(id+"F0.wireOp",EDGE,"E7.right"),sQuery(id+"F0.wireOp",EDGE,"E9"),sQuery(id+"F0.wireOp",EDGE,"E19"),sQuery(id+"F0.wireOp",EDGE,"E20"),sQuery(id+"F0.wireOp",EDGE,"E21"),sQuery(id+"F0.wireOp",EDGE,"E22"),sQuery(id+"F0.wireOp",EDGE,"E23"),sQuery(id+"F0.wireOp",EDGE,"E24.MirrorCS"),sQuery(id+"F0.wireOp",EDGE,"E25.MirrorCS"),sQuery(id+"F0.wireOp",EDGE,"E26.filletArc"),sQuery(id+"F0.wireOp",EDGE,"E27.filletArc"),sQuery(id+"F0.wireOp",EDGE,"E30.top"),sQuery(id+"F0.wireOp",EDGE,"E31"),sQuery(id+"F0.wireOp",EDGE,"E32"),sQuery(id+"F0.wireOp",EDGE,"E34"),sQuery(id+"F0.wireOp",EDGE,"E35"),sQuery(id+"F0.wireOp",EDGE,"E36"),sQuery(id+"F0.wireOp",EDGE,"E37"),sQuery(id+"F0.wireOp",EDGE,"E38"),sQuery(id+"F0.wireOp",EDGE,"E40"),sQuery(id+"F0.wireOp",EDGE,"E41"),sQuery(id+"F0.wireOp",EDGE,"E42.MirrorC")])],"isStart":true}),"instanceName":"1"});
            var sketch = newSketch(context, id + "F16", { "sketchPlane" : qUnion([Q0])});
            skCircle(sketch, "E130.0", {"center": v(-30, 20) * mm, "radius": 2 * mm, "construction": true});
            skCircle(sketch, "E131", {"center": v(21.73, 5.82) * mm, "radius": 2 * mm});
            skLineSegment(sketch, "E132", {"start": v(21.73, 5.82) * mm, "end": v(0, 0) * mm, "construction": true});
            skArc(sketch, "E133", {"start": v(24.34, 2.8) * mm, "mid": v(25.52, 7.12) * mm, "end": v(21.94, 9.82) * mm});
            skLineSegment(sketch, "E134", {"start": v(9, 10.5) * mm, "end": v(21.94, 9.82) * mm});
            skLineSegment(sketch, "E135", {"start": v(8.9, -10.5) * mm, "end": v(24.34, 2.8) * mm});
            skArc(sketch, "E136", {"start": v(14.36, -17.18) * mm, "mid": v(17.04, -17.56) * mm, "end": v(17.65, -14.92) * mm});
            skLineSegment(sketch, "E137", {"start": v(0, 0) * mm, "end": v(15.9, -15.9) * mm, "construction": true});
            skLineSegment(sketch, "E138", {"start": v(8.9, -10.5) * mm, "end": v(14.36, -17.18) * mm});
            skLineSegment(sketch, "E139", {"start": v(9, 0.27) * mm, "end": v(17.65, -14.92) * mm});
            skSolve(sketch);
        }
        {
            var Q0;
            Q0=makeQuery(id+"F16.imprint","IMPRINT",FACE,{"disambiguationData":[TD([[makeQuery(id+"F16.imprint","IMPRINT",EDGE,{"derivedFrom":sQuery(id+"F16.wireOp",EDGE,"E131")}),-1.0]])]});
            var Q1;
            {var subQ0=sQuery(id+"F16.wireOp",EDGE,"E135");var subQ5=sQuery(id+"F16.wireOp",EDGE,"E139");var subQ6=makeQuery(id+"F16.imprint","INTERSECT",VERTEX,{"derivedFrom":[subQ0,subQ5]});Q1=makeQuery(id+"F16.imprint","IMPRINT",FACE,{"disambiguationData":[TD([[makeQuery(id+"F16.imprint","IMPRINT",EDGE,{"disambiguationData":[TD([[subQ6,1.0]])],"derivedFrom":subQ5}),-1.0]])]});}
            var Q2;
            {var subQ0=sQuery(id+"F14.wireOp",EDGE,"E128.right");var subQ1=sQuery(id+"F14.wireOp",EDGE,"E128.top");var subQ2=makeQuery(id+"F14.imprint","INTERSECT",VERTEX,{"derivedFrom":[subQ1,subQ0]});Q2=makeQuery(id+"F14.imprint","IMPRINT",FACE,{"disambiguationData":[TD([[makeQuery(id+"F14.imprint","IMPRINT",EDGE,{"disambiguationData":[TD([[subQ2,1.0]])],"derivedFrom":subQ1}),-1.0]])]});}
            extrude(context, id + "F17", {"entities" : qUnion([Q0, Q1, Q2]), "operationType" : NewBodyOperationType.ADD, "oppositeDirection" : true, "depth" : 1.5 * mm, "offsetDistance" : 25 * mm});
        }
        {
            var Q0;
            {var subQ0=sQuery(id+"F0.wireOp",EDGE,"E42.MirrorC");var subQ1=sQuery(id+"F0.wireOp",EDGE,"E41");var subQ2=sQuery(id+"F0.wireOp",EDGE,"E40");var subQ3=sQuery(id+"F0.wireOp",EDGE,"E38");var subQ4=sQuery(id+"F0.wireOp",EDGE,"E37");var subQ5=sQuery(id+"F0.wireOp",EDGE,"E36");var subQ6=sQuery(id+"F0.wireOp",EDGE,"E35");var subQ7=sQuery(id+"F0.wireOp",EDGE,"E34");var subQ8=sQuery(id+"F0.wireOp",EDGE,"E32");var subQ9=sQuery(id+"F0.wireOp",EDGE,"E31");var subQ10=sQuery(id+"F0.wireOp",EDGE,"E30.top");var subQ11=sQuery(id+"F0.wireOp",EDGE,"E27.filletArc");var subQ12=sQuery(id+"F0.wireOp",EDGE,"E26.filletArc");var subQ13=sQuery(id+"F0.wireOp",EDGE,"E25.MirrorCS");var subQ14=sQuery(id+"F0.wireOp",EDGE,"E24.MirrorCS");var subQ15=sQuery(id+"F0.wireOp",EDGE,"E23");var subQ16=sQuery(id+"F0.wireOp",EDGE,"E22");var subQ17=sQuery(id+"F0.wireOp",EDGE,"E21");var subQ18=sQuery(id+"F0.wireOp",EDGE,"E20");var subQ19=sQuery(id+"F0.wireOp",EDGE,"E19");var subQ20=sQuery(id+"F0.wireOp",EDGE,"E9");var subQ21=sQuery(id+"F0.wireOp",EDGE,"E7.right");var subQ22=sQuery(id+"F0.wireOp",EDGE,"E7.top");var subQ23=sQuery(id+"F0.wireOp",EDGE,"E6.MirrorC");var subQ24=sQuery(id+"F0.wireOp",EDGE,"E5.MirrorC");var subQ25=sQuery(id+"F0.wireOp",EDGE,"E4");var subQ26=sQuery(id+"F0.wireOp",EDGE,"E1");var subQ27=sQuery(id+"F0.wireOp",EDGE,"E0");Q0=makeQuery(id+"F17.boolean.opBoolean","MERGE",FACE,{"derivedFrom":[makeQuery(id+"F13.opPattern","COPY",FACE,{"derivedFrom":makeQuery(id+"F1.opExtrude","CAP_FACE",FACE,{"disambiguationData":[OSD([subQ27,subQ26,subQ25,subQ24,subQ23,subQ21,subQ20,subQ19,subQ18,subQ17,subQ16,subQ15,subQ14,subQ13,subQ12,subQ11,subQ10,subQ9,subQ8,subQ7,subQ6,subQ5,subQ4,subQ3,subQ2,subQ1,subQ0])],"isStart":true}),"instanceName":"1"}),makeQuery(id+"F17.opExtrude","CAP_FACE",FACE,{"disambiguationData":[OSD([subQ27,subQ26,subQ25,subQ24,subQ23,subQ22,sQuery(id+"F0.wireOp",EDGE,"E7.left"),subQ21,subQ20,subQ19,subQ18,subQ17,subQ16,subQ15,subQ14,subQ13,subQ12,subQ11,subQ10,subQ9,subQ8,subQ7,subQ6,subQ5,subQ4,subQ3,subQ2,subQ1,subQ0,sQuery(id+"F14.wireOp",EDGE,"E128.top"),sQuery(id+"F14.wireOp",EDGE,"E128.right")])],"isStart":true}),makeQuery(id+"F17.opExtrude","CAP_FACE",FACE,{"disambiguationData":[OSD([subQ27,subQ26,subQ25,subQ24,subQ23,subQ22,subQ21,subQ20,subQ19,subQ18,subQ17,subQ16,subQ15,subQ14,subQ13,subQ12,subQ11,subQ10,subQ9,subQ8,subQ7,subQ6,subQ5,subQ4,subQ3,subQ2,subQ1,subQ0,sQuery(id+"F16.wireOp",EDGE,"E131"),sQuery(id+"F16.wireOp",EDGE,"E133"),sQuery(id+"F16.wireOp",EDGE,"E134"),sQuery(id+"F16.wireOp",EDGE,"E135")])],"isStart":true})]});}
            var sketch = newSketch(context, id + "F18", { "sketchPlane" : qUnion([Q0])});
            skLineSegment(sketch, "E140", {"start": v(-32, -10.5) * mm, "end": v(-41.1, -5.25) * mm});
            skLineSegment(sketch, "E141", {"start": v(-41.1, -5.25) * mm, "end": v(-32, 10.5) * mm});
            skLineSegment(sketch, "E142", {"start": v(-32, 10.5) * mm, "end": v(-32, -10.5) * mm});
            skLineSegment(sketch, "E143", {"start": v(-32, 10.5) * mm, "end": v(-34.6, 12) * mm});
            skLineSegment(sketch, "E144", {"start": v(-34.6, 12) * mm, "end": v(-43.7, -3.75) * mm});
            skLineSegment(sketch, "E145", {"start": v(-43.7, -3.75) * mm, "end": v(-41.1, -5.25) * mm});
            skLineSegment(sketch, "E146", {"start": v(-33.3, 11.25) * mm, "end": v(-42.4, -4.5) * mm, "construction": true});
            skLineSegment(sketch, "E147", {"start": v(-39.14, 4.12) * mm, "end": v(-36.55, 2.63) * mm, "construction": true});
            skCircle(sketch, "E148", {"center": v(-34.72, 8.79) * mm, "radius": 1 * mm});
            skCircle(sketch, "E149.MirrorC", {"center": v(-40.97, -2.04) * mm, "radius": 1 * mm});
            skCircle(sketch, "E150", {"center": v(-37.85, 3.37) * mm, "radius": 1 * mm});
            skLineSegment(sketch, "E151", {"start": v(-34.6, 12) * mm, "end": v(-34.6, 12) * mm});
            skLineSegment(sketch, "E152", {"start": v(-35.96, 11.63) * mm, "end": v(-44.06, -2.38) * mm});
            skLineSegment(sketch, "E153", {"start": v(-43.7, -3.75) * mm, "end": v(-43.7, -3.75) * mm});
            skPoint(sketch, "E154.visualSharp", {"position": v(-35.46, 12.5) * mm});
            skArc(sketch, "E154.filletArc", {"start": v(-34.6, 12) * mm, "mid": v(-35.36, 12.1) * mm, "end": v(-35.96, 11.63) * mm});
            skPoint(sketch, "E155.visualSharp", {"position": v(-44.56, -3.25) * mm});
            skArc(sketch, "E155.filletArc", {"start": v(-44.06, -2.38) * mm, "mid": v(-44.16, -3.14) * mm, "end": v(-43.7, -3.75) * mm});
            skSolve(sketch);
        }
        {
            var Q0;
            Q0 = qSketchRegion(id + "F18", true);
            extrude(context, id + "F19", {"entities" : qUnion([Q0]), "operationType" : NewBodyOperationType.ADD, "oppositeDirection" : true, "depth" : 1.5 * mm, "offsetDistance" : 25 * mm});
        }
        {
            var Q0;
            {var subQ0=sQuery(id+"F0.wireOp",EDGE,"E42.MirrorC");var subQ1=sQuery(id+"F0.wireOp",EDGE,"E41");var subQ2=sQuery(id+"F0.wireOp",EDGE,"E40");var subQ3=sQuery(id+"F0.wireOp",EDGE,"E38");var subQ4=sQuery(id+"F0.wireOp",EDGE,"E37");var subQ5=sQuery(id+"F0.wireOp",EDGE,"E36");var subQ6=sQuery(id+"F0.wireOp",EDGE,"E35");var subQ7=sQuery(id+"F0.wireOp",EDGE,"E34");var subQ8=sQuery(id+"F0.wireOp",EDGE,"E32");var subQ9=sQuery(id+"F0.wireOp",EDGE,"E31");var subQ10=sQuery(id+"F0.wireOp",EDGE,"E30.top");var subQ11=sQuery(id+"F0.wireOp",EDGE,"E27.filletArc");var subQ12=sQuery(id+"F0.wireOp",EDGE,"E26.filletArc");var subQ13=sQuery(id+"F0.wireOp",EDGE,"E25.MirrorCS");var subQ14=sQuery(id+"F0.wireOp",EDGE,"E24.MirrorCS");var subQ15=sQuery(id+"F0.wireOp",EDGE,"E23");var subQ16=sQuery(id+"F0.wireOp",EDGE,"E22");var subQ17=sQuery(id+"F0.wireOp",EDGE,"E21");var subQ18=sQuery(id+"F0.wireOp",EDGE,"E20");var subQ19=sQuery(id+"F0.wireOp",EDGE,"E19");var subQ20=sQuery(id+"F0.wireOp",EDGE,"E9");var subQ21=sQuery(id+"F0.wireOp",EDGE,"E7.right");var subQ22=sQuery(id+"F0.wireOp",EDGE,"E7.top");var subQ23=sQuery(id+"F0.wireOp",EDGE,"E6.MirrorC");var subQ24=sQuery(id+"F0.wireOp",EDGE,"E5.MirrorC");var subQ25=sQuery(id+"F0.wireOp",EDGE,"E4");var subQ26=sQuery(id+"F0.wireOp",EDGE,"E1");var subQ27=sQuery(id+"F0.wireOp",EDGE,"E0");Q0=makeQuery(id+"F19.boolean.opBoolean","MERGE",FACE,{"derivedFrom":[makeQuery(id+"F17.boolean.opBoolean","MERGE",FACE,{"derivedFrom":[makeQuery(id+"F13.opPattern","COPY",FACE,{"derivedFrom":makeQuery(id+"F1.opExtrude","CAP_FACE",FACE,{"disambiguationData":[OSD([subQ27,subQ26,subQ25,subQ24,subQ23,subQ21,subQ20,subQ19,subQ18,subQ17,subQ16,subQ15,subQ14,subQ13,subQ12,subQ11,subQ10,subQ9,subQ8,subQ7,subQ6,subQ5,subQ4,subQ3,subQ2,subQ1,subQ0])],"isStart":true}),"instanceName":"1"}),makeQuery(id+"F17.opExtrude","CAP_FACE",FACE,{"disambiguationData":[OSD([subQ27,subQ26,subQ25,subQ24,subQ23,subQ22,sQuery(id+"F0.wireOp",EDGE,"E7.left"),subQ21,subQ20,subQ19,subQ18,subQ17,subQ16,subQ15,subQ14,subQ13,subQ12,subQ11,subQ10,subQ9,subQ8,subQ7,subQ6,subQ5,subQ4,subQ3,subQ2,subQ1,subQ0,sQuery(id+"F14.wireOp",EDGE,"E128.top"),sQuery(id+"F14.wireOp",EDGE,"E128.right")])],"isStart":true}),makeQuery(id+"F17.opExtrude","CAP_FACE",FACE,{"disambiguationData":[OSD([subQ27,subQ26,subQ25,subQ24,subQ23,subQ22,subQ21,subQ20,subQ19,subQ18,subQ17,subQ16,subQ15,subQ14,subQ13,subQ12,subQ11,subQ10,subQ9,subQ8,subQ7,subQ6,subQ5,subQ4,subQ3,subQ2,subQ1,subQ0,sQuery(id+"F16.wireOp",EDGE,"E131"),sQuery(id+"F16.wireOp",EDGE,"E133"),sQuery(id+"F16.wireOp",EDGE,"E134"),sQuery(id+"F16.wireOp",EDGE,"E135")])],"isStart":true})]}),makeQuery(id+"F19.opExtrude","CAP_FACE",FACE,{"disambiguationData":[OSD([sQuery(id+"F18.wireOp",EDGE,"E140"),sQuery(id+"F18.wireOp",EDGE,"E142"),sQuery(id+"F18.wireOp",EDGE,"E143"),sQuery(id+"F18.wireOp",EDGE,"E145"),sQuery(id+"F18.wireOp",EDGE,"E148"),sQuery(id+"F18.wireOp",EDGE,"E149.MirrorC"),sQuery(id+"F18.wireOp",EDGE,"E150"),sQuery(id+"F18.wireOp",EDGE,"E152"),sQuery(id+"F18.wireOp",EDGE,"E154.filletArc"),sQuery(id+"F18.wireOp",EDGE,"E155.filletArc")])],"isStart":true})]});}
            var sketch = newSketch(context, id + "F20", { "sketchPlane" : qUnion([Q0])});
            skCircle(sketch, "E156.0", {"center": v(21.73, 5.82) * mm, "radius": 2 * mm});
            skCircle(sketch, "E157", {"center": v(21.73, 5.82) * mm, "radius": 1.5 * mm});
            skSolve(sketch);
        }
        {
            var Q0;
            Q0 = qSketchRegion(id + "F20", true);
            extrude(context, id + "F21", {"entities" : qUnion([Q0]), "operationType" : NewBodyOperationType.ADD, "oppositeDirection" : true, "depth" : 1.5 * mm, "offsetDistance" : 25 * mm});
        }
    });
